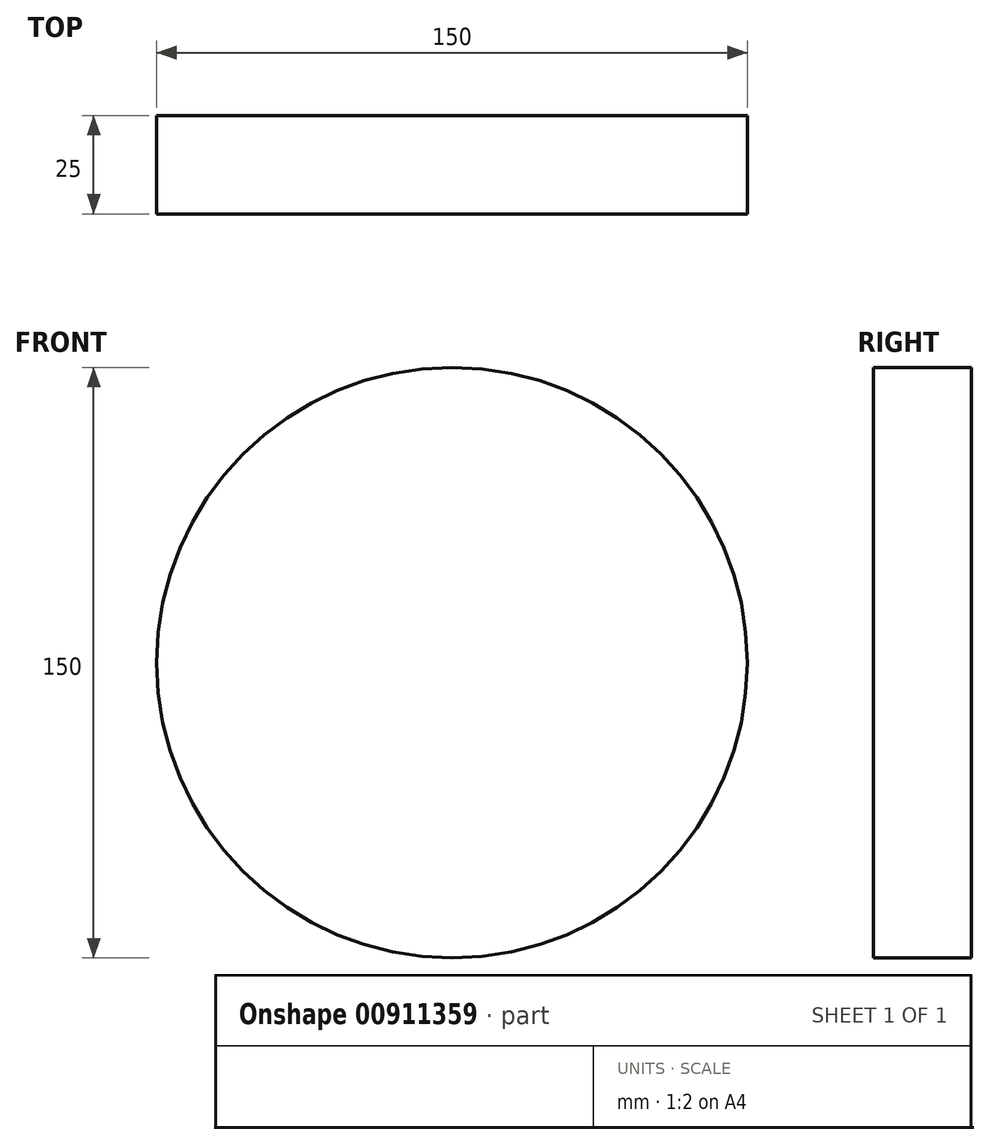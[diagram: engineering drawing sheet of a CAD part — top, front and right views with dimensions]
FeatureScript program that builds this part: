
annotation { "Feature Type Name" : "Feature", "Feature Type Description" : "" }
export const myFeature = defineFeature(function(context is Context, id is Id, definition is map)
    precondition{}
    {
        {
            var Q0;
            Q0=qCreatedBy(makeId("Front.planeOp"),FACE);
            var sketch = newSketch(context, id + "F0", { "sketchPlane" : qUnion([Q0])});
            skCircle(sketch, "E0", {"center": v(0, 0) * mm, "radius": 75 * mm});
            skSolve(sketch);
        }
        {
            var Q0;
            Q0=makeQuery(id+"F0.imprint","IMPRINT",FACE,{"disambiguationData":[TD([[makeQuery(id+"F0.imprint","IMPRINT",EDGE,{"derivedFrom":sQuery(id+"F0.wireOp",EDGE,"E0")}),1.0]])]});
            extrude(context, id + "F1", {"entities" : qUnion([Q0]), "depth" : 25 * mm, "offsetDistance" : 25 * mm});
        }
    });
